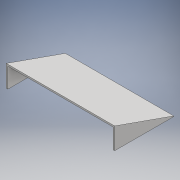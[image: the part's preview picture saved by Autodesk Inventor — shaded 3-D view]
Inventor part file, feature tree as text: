
AUTODESK INVENTOR PART (.ipt)
format: ipt  version: 2018.2 (Build 222227000, 227)  size: 126,464 bytes
history: native  units: mm
features: extrude x4, sketch x4
ambient origin geometry x8: Origin, YZ Plane, XZ Plane, XY Plane, X Axis, Y Axis, Z Axis, Center Point
bodies: Solid1 (feature_tree)
feature tree (8):
  extrude  "Extrusion1"  Depth=156.0mm
  extrude  "Extrusion2"  Depth=2.4mm
  extrude  "Extrusion3"  Depth=151.2mm TaperAngle=0.0deg
  extrude  "Extrusion4"  Depth=2.4mm TaperAngle=0.0deg
  sketch  "Sketch1"  dims[d0=85.0mm d1=156.0mm]
  sketch  "Sketch2"  dims[d2=2.4mm d3=82.6mm]
  sketch  "Sketch3"  dims[d4=151.2mm d5=0.9mm d6=0.0mm]
  sketch  "Sketch4"  dims[d7=30.0mm d8=2.4mm d9=0.0mm d10=2.4mm d11=0.0mm d12=2.4mm d13=152.0mm d14=0.0mm]
